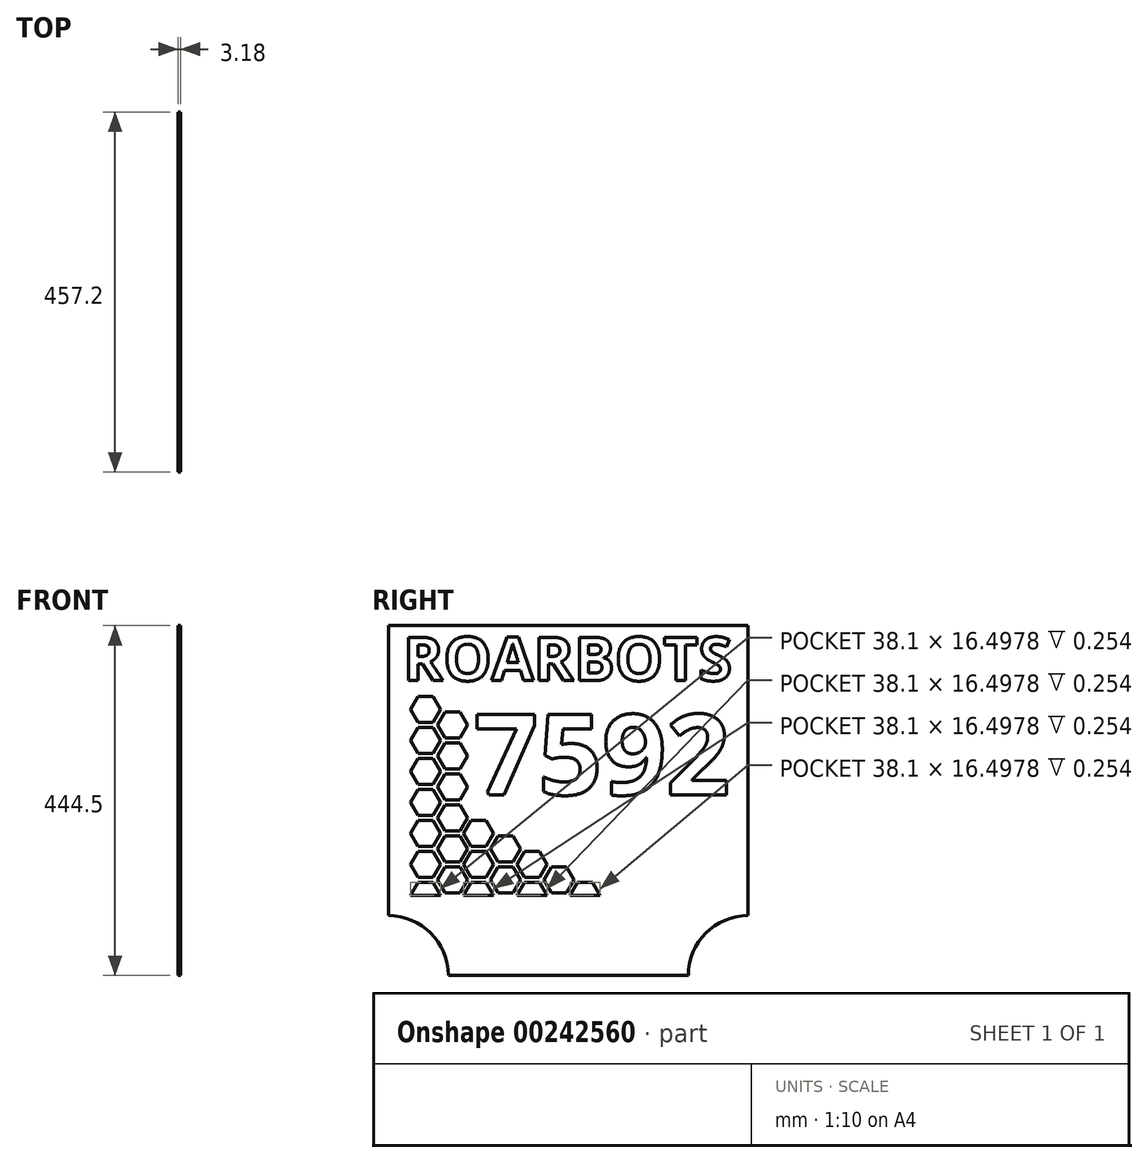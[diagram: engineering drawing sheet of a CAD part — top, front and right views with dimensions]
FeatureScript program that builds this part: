
annotation { "Feature Type Name" : "Feature", "Feature Type Description" : "" }
export const myFeature = defineFeature(function(context is Context, id is Id, definition is map)
    precondition{}
    {
        {
            var Q0;
            Q0=qCreatedBy(makeId("Right.planeOp"),FACE);
            var sketch = newSketch(context, id + "F0", { "sketchPlane" : qUnion([Q0])});
            skLineSegment(sketch, "E0.bottom", {"start": v(228.6, 222.25) * mm, "end": v(-228.6, 222.25) * mm, "construction": true});
            skLineSegment(sketch, "E0.top", {"start": v(228.6, -222.25) * mm, "end": v(-228.6, -222.25) * mm, "construction": true});
            skLineSegment(sketch, "E0.left", {"start": v(228.6, 222.25) * mm, "end": v(228.6, -222.25) * mm, "construction": true});
            skLineSegment(sketch, "E0.right", {"start": v(-228.6, 222.25) * mm, "end": v(-228.6, -222.25) * mm, "construction": true});
            skPoint(sketch, "E0.middle", {"position": v(0, 0) * mm});
            skLineSegment(sketch, "E1.bottom", {"start": v(-228.6, -222.25) * mm, "end": v(228.6, -222.25) * mm});
            skLineSegment(sketch, "E1.top", {"start": v(-228.6, 222.25) * mm, "end": v(228.6, 222.25) * mm});
            skLineSegment(sketch, "E1.left", {"start": v(-228.6, -222.25) * mm, "end": v(-228.6, 222.25) * mm});
            skLineSegment(sketch, "E1.right", {"start": v(228.6, -222.25) * mm, "end": v(228.6, 222.25) * mm});
            skCircle(sketch, "E2", {"center": v(-228.6, -222.25) * mm, "radius": 76.2 * mm});
            skCircle(sketch, "E3", {"center": v(228.6, -222.25) * mm, "radius": 76.2 * mm});
            skSolve(sketch);
        }
        {
            var Q0;
            {var subQ1=sQuery(id+"F0.wireOp",EDGE,"E1.top");Q0=makeQuery(id+"F0.imprint","IMPRINT",FACE,{"disambiguationData":[TD([[makeQuery(id+"F0.imprint","IMPRINT",EDGE,{"derivedFrom":subQ1}),-1.0]])]});}
            extrude(context, id + "F1", {"entities" : qUnion([Q0]), "depth" : 3.17 * mm});
        }
        {
            var Q0;
            Q0=makeQuery(id+"F1.opExtrude","CAP_FACE",FACE,{"disambiguationData":[OSD([sQuery(id+"F0.wireOp",EDGE,"E1.bottom"),sQuery(id+"F0.wireOp",EDGE,"E1.top"),sQuery(id+"F0.wireOp",EDGE,"E1.left"),sQuery(id+"F0.wireOp",EDGE,"E1.right")])],"isStart":false});
            var sketch = newSketch(context, id + "F2", { "sketchPlane" : qUnion([Q0])});
            skLineSegment(sketch, "E4", {"start": v(-228.6, -120.65) * mm, "end": v(228.6, -120.65) * mm});
            skCircle(sketch, "E5.cCircle", {"center": v(-181.28, -120.65) * mm, "radius": 19.05 * mm, "construction": true});
            skLineSegment(sketch, "E5.0", {"start": v(-162.23, -120.65) * mm, "end": v(-171.75, -137.15) * mm});
            skLineSegment(sketch, "E5.1", {"start": v(-171.75, -137.15) * mm, "end": v(-190.8, -137.15) * mm});
            skLineSegment(sketch, "E5.2", {"start": v(-190.8, -137.15) * mm, "end": v(-200.33, -120.65) * mm});
            skLineSegment(sketch, "E5.3", {"start": v(-200.33, -120.65) * mm, "end": v(-190.8, -104.15) * mm});
            skLineSegment(sketch, "E5.4", {"start": v(-190.8, -104.15) * mm, "end": v(-171.75, -104.15) * mm});
            skLineSegment(sketch, "E5.5", {"start": v(-171.75, -104.15) * mm, "end": v(-162.23, -120.65) * mm});
            skLineSegment(sketch, "E6", {"start": v(-228.6, -137.15) * mm, "end": v(228.6, -137.15) * mm});
            skCircle(sketch, "E7.cCircle", {"center": v(-147.2, -100.98) * mm, "radius": 19.05 * mm, "construction": true});
            skLineSegment(sketch, "E7.0", {"start": v(-137.68, -117.48) * mm, "end": v(-156.73, -117.48) * mm});
            skLineSegment(sketch, "E7.1", {"start": v(-156.73, -117.48) * mm, "end": v(-166.25, -100.98) * mm});
            skLineSegment(sketch, "E7.2", {"start": v(-166.25, -100.98) * mm, "end": v(-156.73, -84.48) * mm});
            skLineSegment(sketch, "E7.3", {"start": v(-156.73, -84.48) * mm, "end": v(-137.68, -84.48) * mm});
            skLineSegment(sketch, "E7.4", {"start": v(-137.68, -84.48) * mm, "end": v(-128.15, -100.98) * mm});
            skLineSegment(sketch, "E7.5", {"start": v(-128.15, -100.98) * mm, "end": v(-137.68, -117.48) * mm});
            skLineSegment(sketch, "E8", {"start": v(-181.28, -120.65) * mm, "end": v(-147.2, -100.98) * mm});
            skLineSegment(sketch, "E9.1.0.0", {"start": v(-94.66, -120.65) * mm, "end": v(-104.19, -137.15) * mm});
            skLineSegment(sketch, "E9.1.0.1", {"start": v(-104.19, -137.15) * mm, "end": v(-123.24, -137.15) * mm});
            skLineSegment(sketch, "E9.1.0.2", {"start": v(-123.24, -137.15) * mm, "end": v(-132.76, -120.65) * mm});
            skLineSegment(sketch, "E9.1.0.3", {"start": v(-132.76, -120.65) * mm, "end": v(-123.24, -104.15) * mm});
            skLineSegment(sketch, "E9.1.0.4", {"start": v(-123.24, -104.15) * mm, "end": v(-104.19, -104.15) * mm});
            skLineSegment(sketch, "E9.1.0.5", {"start": v(-104.19, -104.15) * mm, "end": v(-94.66, -120.65) * mm});
            skLineSegment(sketch, "E9.1.0.6", {"start": v(-70.11, -117.48) * mm, "end": v(-89.16, -117.48) * mm});
            skLineSegment(sketch, "E9.1.0.7", {"start": v(-89.16, -117.48) * mm, "end": v(-98.69, -100.98) * mm});
            skLineSegment(sketch, "E9.1.0.8", {"start": v(-98.69, -100.98) * mm, "end": v(-89.16, -84.48) * mm});
            skLineSegment(sketch, "E9.1.0.9", {"start": v(-89.16, -84.48) * mm, "end": v(-70.11, -84.48) * mm});
            skLineSegment(sketch, "E9.1.0.10", {"start": v(-70.11, -84.48) * mm, "end": v(-60.59, -100.98) * mm});
            skLineSegment(sketch, "E9.1.0.11", {"start": v(-60.59, -100.98) * mm, "end": v(-70.11, -117.48) * mm});
            skLineSegment(sketch, "E9.2.0.0", {"start": v(-27.1, -120.65) * mm, "end": v(-36.62, -137.15) * mm});
            skLineSegment(sketch, "E9.2.0.1", {"start": v(-36.62, -137.15) * mm, "end": v(-55.67, -137.15) * mm});
            skLineSegment(sketch, "E9.2.0.2", {"start": v(-55.67, -137.15) * mm, "end": v(-65.2, -120.65) * mm});
            skLineSegment(sketch, "E9.2.0.3", {"start": v(-65.2, -120.65) * mm, "end": v(-55.67, -104.15) * mm});
            skLineSegment(sketch, "E9.2.0.4", {"start": v(-55.67, -104.15) * mm, "end": v(-36.62, -104.15) * mm});
            skLineSegment(sketch, "E9.2.0.5", {"start": v(-36.62, -104.15) * mm, "end": v(-27.1, -120.65) * mm});
            skLineSegment(sketch, "E9.2.0.6", {"start": v(-2.55, -117.48) * mm, "end": v(-21.6, -117.48) * mm});
            skLineSegment(sketch, "E9.2.0.7", {"start": v(-21.6, -117.48) * mm, "end": v(-31.12, -100.98) * mm});
            skLineSegment(sketch, "E9.2.0.8", {"start": v(-31.12, -100.98) * mm, "end": v(-21.6, -84.48) * mm});
            skLineSegment(sketch, "E9.2.0.9", {"start": v(-21.6, -84.48) * mm, "end": v(-2.55, -84.48) * mm});
            skLineSegment(sketch, "E9.2.0.10", {"start": v(-2.55, -84.48) * mm, "end": v(6.98, -100.98) * mm});
            skLineSegment(sketch, "E9.2.0.11", {"start": v(6.98, -100.98) * mm, "end": v(-2.55, -117.48) * mm});
            skLineSegment(sketch, "E9.3.0.0", {"start": v(40.47, -120.65) * mm, "end": v(30.94, -137.15) * mm});
            skLineSegment(sketch, "E9.3.0.1", {"start": v(30.94, -137.15) * mm, "end": v(11.9, -137.15) * mm});
            skLineSegment(sketch, "E9.3.0.2", {"start": v(11.9, -137.15) * mm, "end": v(2.37, -120.65) * mm});
            skLineSegment(sketch, "E9.3.0.3", {"start": v(2.37, -120.65) * mm, "end": v(11.9, -104.15) * mm});
            skLineSegment(sketch, "E9.3.0.4", {"start": v(11.9, -104.15) * mm, "end": v(30.94, -104.15) * mm});
            skLineSegment(sketch, "E9.3.0.5", {"start": v(30.94, -104.15) * mm, "end": v(40.47, -120.65) * mm});
            skLineSegment(sketch, "E9.3.0.6", {"start": v(65.02, -117.48) * mm, "end": v(45.97, -117.48) * mm});
            skLineSegment(sketch, "E9.3.0.7", {"start": v(45.97, -117.48) * mm, "end": v(36.44, -100.98) * mm});
            skLineSegment(sketch, "E9.3.0.8", {"start": v(36.44, -100.98) * mm, "end": v(45.97, -84.48) * mm});
            skLineSegment(sketch, "E9.3.0.9", {"start": v(45.97, -84.48) * mm, "end": v(65.02, -84.48) * mm});
            skLineSegment(sketch, "E9.3.0.10", {"start": v(65.02, -84.48) * mm, "end": v(74.54, -100.98) * mm});
            skLineSegment(sketch, "E9.3.0.11", {"start": v(74.54, -100.98) * mm, "end": v(65.02, -117.48) * mm});
            skLineSegment(sketch, "E9.direction1", {"start": v(-171.75, -137.15) * mm, "end": v(-104.19, -137.15) * mm, "construction": true});
            skLineSegment(sketch, "E10.0.1.0", {"start": v(-162.23, -81.28) * mm, "end": v(-171.75, -97.78) * mm});
            skLineSegment(sketch, "E10.0.1.1", {"start": v(-190.8, -97.78) * mm, "end": v(-200.33, -81.28) * mm});
            skLineSegment(sketch, "E10.0.1.2", {"start": v(-200.33, -81.28) * mm, "end": v(-190.8, -64.78) * mm});
            skLineSegment(sketch, "E10.0.1.3", {"start": v(-190.8, -64.78) * mm, "end": v(-171.75, -64.78) * mm});
            skLineSegment(sketch, "E10.0.1.4", {"start": v(-171.75, -64.78) * mm, "end": v(-162.23, -81.28) * mm});
            skLineSegment(sketch, "E10.0.1.5", {"start": v(-137.68, -78.1) * mm, "end": v(-156.73, -78.1) * mm});
            skLineSegment(sketch, "E10.0.1.6", {"start": v(-156.73, -78.1) * mm, "end": v(-166.25, -61.6) * mm});
            skLineSegment(sketch, "E10.0.1.7", {"start": v(-166.25, -61.6) * mm, "end": v(-156.73, -45.1) * mm});
            skLineSegment(sketch, "E10.0.1.8", {"start": v(-156.73, -45.1) * mm, "end": v(-137.68, -45.1) * mm});
            skLineSegment(sketch, "E10.0.1.9", {"start": v(-137.68, -45.1) * mm, "end": v(-128.15, -61.6) * mm});
            skLineSegment(sketch, "E10.0.1.10", {"start": v(-128.15, -61.6) * mm, "end": v(-137.68, -78.1) * mm});
            skLineSegment(sketch, "E10.0.1.11", {"start": v(-132.76, -81.28) * mm, "end": v(-123.24, -64.78) * mm});
            skLineSegment(sketch, "E10.0.1.12", {"start": v(-123.24, -64.78) * mm, "end": v(-104.19, -64.78) * mm});
            skLineSegment(sketch, "E10.0.1.13", {"start": v(-104.19, -64.78) * mm, "end": v(-94.66, -81.28) * mm});
            skLineSegment(sketch, "E10.0.1.14", {"start": v(-94.66, -81.28) * mm, "end": v(-104.19, -97.78) * mm});
            skLineSegment(sketch, "E10.0.1.15", {"start": v(-123.24, -97.78) * mm, "end": v(-132.76, -81.28) * mm});
            skLineSegment(sketch, "E10.0.1.16", {"start": v(-89.16, -78.1) * mm, "end": v(-98.69, -61.6) * mm});
            skLineSegment(sketch, "E10.0.1.17", {"start": v(-98.69, -61.6) * mm, "end": v(-89.16, -45.1) * mm});
            skLineSegment(sketch, "E10.0.1.18", {"start": v(-89.16, -45.1) * mm, "end": v(-70.11, -45.1) * mm});
            skLineSegment(sketch, "E10.0.1.19", {"start": v(-70.11, -45.1) * mm, "end": v(-60.59, -61.6) * mm});
            skLineSegment(sketch, "E10.0.1.20", {"start": v(-60.59, -61.6) * mm, "end": v(-70.11, -78.1) * mm});
            skLineSegment(sketch, "E10.0.1.21", {"start": v(-70.11, -78.1) * mm, "end": v(-89.16, -78.1) * mm});
            skLineSegment(sketch, "E10.0.1.22", {"start": v(-55.67, -97.78) * mm, "end": v(-65.2, -81.28) * mm});
            skLineSegment(sketch, "E10.0.1.23", {"start": v(-65.2, -81.28) * mm, "end": v(-55.67, -64.78) * mm});
            skLineSegment(sketch, "E10.0.1.24", {"start": v(-55.67, -64.78) * mm, "end": v(-36.62, -64.78) * mm});
            skLineSegment(sketch, "E10.0.1.25", {"start": v(-36.62, -64.78) * mm, "end": v(-27.1, -81.28) * mm});
            skLineSegment(sketch, "E10.0.1.26", {"start": v(-27.1, -81.28) * mm, "end": v(-36.62, -97.78) * mm});
            skLineSegment(sketch, "E10.0.1.27", {"start": v(-21.6, -78.1) * mm, "end": v(-31.12, -61.6) * mm});
            skLineSegment(sketch, "E10.0.1.28", {"start": v(-31.12, -61.6) * mm, "end": v(-21.6, -45.1) * mm});
            skLineSegment(sketch, "E10.0.1.29", {"start": v(-21.6, -45.1) * mm, "end": v(-2.55, -45.1) * mm});
            skLineSegment(sketch, "E10.0.1.30", {"start": v(-2.55, -45.1) * mm, "end": v(6.98, -61.6) * mm});
            skLineSegment(sketch, "E10.0.1.31", {"start": v(6.98, -61.6) * mm, "end": v(-2.55, -78.1) * mm});
            skLineSegment(sketch, "E10.0.1.32", {"start": v(2.37, -81.28) * mm, "end": v(11.9, -64.78) * mm});
            skLineSegment(sketch, "E10.0.1.33", {"start": v(11.9, -64.78) * mm, "end": v(30.94, -64.78) * mm});
            skLineSegment(sketch, "E10.0.1.34", {"start": v(30.94, -64.78) * mm, "end": v(40.47, -81.28) * mm});
            skLineSegment(sketch, "E10.0.1.35", {"start": v(40.47, -81.28) * mm, "end": v(30.94, -97.78) * mm});
            skLineSegment(sketch, "E10.0.1.36", {"start": v(11.9, -97.78) * mm, "end": v(2.37, -81.28) * mm});
            skLineSegment(sketch, "E10.0.2.0", {"start": v(-162.23, -41.91) * mm, "end": v(-171.75, -58.4) * mm});
            skLineSegment(sketch, "E10.0.2.1", {"start": v(-190.8, -58.4) * mm, "end": v(-200.33, -41.91) * mm});
            skLineSegment(sketch, "E10.0.2.2", {"start": v(-200.33, -41.91) * mm, "end": v(-190.8, -25.41) * mm});
            skLineSegment(sketch, "E10.0.2.3", {"start": v(-190.8, -25.41) * mm, "end": v(-171.75, -25.41) * mm});
            skLineSegment(sketch, "E10.0.2.4", {"start": v(-171.75, -25.41) * mm, "end": v(-162.23, -41.91) * mm});
            skLineSegment(sketch, "E10.0.2.5", {"start": v(-137.68, -38.74) * mm, "end": v(-156.73, -38.74) * mm});
            skLineSegment(sketch, "E10.0.2.6", {"start": v(-156.73, -38.74) * mm, "end": v(-166.25, -22.24) * mm});
            skLineSegment(sketch, "E10.0.2.7", {"start": v(-166.25, -22.24) * mm, "end": v(-156.73, -5.74) * mm});
            skLineSegment(sketch, "E10.0.2.8", {"start": v(-156.73, -5.74) * mm, "end": v(-137.68, -5.74) * mm});
            skLineSegment(sketch, "E10.0.2.9", {"start": v(-137.68, -5.74) * mm, "end": v(-128.15, -22.24) * mm});
            skLineSegment(sketch, "E10.0.2.10", {"start": v(-128.15, -22.24) * mm, "end": v(-137.68, -38.74) * mm});
            skLineSegment(sketch, "E10.0.2.11", {"start": v(-132.76, -41.91) * mm, "end": v(-123.24, -25.41) * mm});
            skLineSegment(sketch, "E10.0.2.12", {"start": v(-123.24, -25.41) * mm, "end": v(-104.19, -25.41) * mm});
            skLineSegment(sketch, "E10.0.2.13", {"start": v(-104.19, -25.41) * mm, "end": v(-94.66, -41.91) * mm});
            skLineSegment(sketch, "E10.0.2.14", {"start": v(-94.66, -41.91) * mm, "end": v(-104.19, -58.4) * mm});
            skLineSegment(sketch, "E10.0.2.15", {"start": v(-123.24, -58.4) * mm, "end": v(-132.76, -41.9) * mm});
            skLineSegment(sketch, "E10.0.2.16", {"start": v(-89.16, -38.74) * mm, "end": v(-98.69, -22.24) * mm});
            skLineSegment(sketch, "E10.0.2.17", {"start": v(-98.69, -22.24) * mm, "end": v(-89.16, -5.74) * mm});
            skLineSegment(sketch, "E10.0.2.18", {"start": v(-89.16, -5.74) * mm, "end": v(-70.11, -5.74) * mm});
            skLineSegment(sketch, "E10.0.2.19", {"start": v(-70.11, -5.74) * mm, "end": v(-60.59, -22.24) * mm});
            skLineSegment(sketch, "E10.0.2.20", {"start": v(-60.59, -22.24) * mm, "end": v(-70.11, -38.74) * mm});
            skLineSegment(sketch, "E10.0.2.21", {"start": v(-70.11, -38.74) * mm, "end": v(-89.16, -38.74) * mm});
            skLineSegment(sketch, "E10.0.2.22", {"start": v(-55.67, -58.4) * mm, "end": v(-65.2, -41.9) * mm});
            skLineSegment(sketch, "E10.0.2.23", {"start": v(-65.2, -41.91) * mm, "end": v(-55.67, -25.41) * mm});
            skLineSegment(sketch, "E10.0.2.24", {"start": v(-55.67, -25.41) * mm, "end": v(-36.62, -25.41) * mm});
            skLineSegment(sketch, "E10.0.2.25", {"start": v(-36.62, -25.41) * mm, "end": v(-27.1, -41.91) * mm});
            skLineSegment(sketch, "E10.0.2.26", {"start": v(-27.1, -41.91) * mm, "end": v(-36.62, -58.4) * mm});
            skLineSegment(sketch, "E10.0.3.0", {"start": v(-162.23, -2.54) * mm, "end": v(-171.75, -19.04) * mm});
            skLineSegment(sketch, "E10.0.3.1", {"start": v(-190.8, -19.04) * mm, "end": v(-200.33, -2.54) * mm});
            skLineSegment(sketch, "E10.0.3.2", {"start": v(-200.33, -2.54) * mm, "end": v(-190.8, 13.96) * mm});
            skLineSegment(sketch, "E10.0.3.3", {"start": v(-190.8, 13.96) * mm, "end": v(-171.75, 13.96) * mm});
            skLineSegment(sketch, "E10.0.3.4", {"start": v(-171.75, 13.96) * mm, "end": v(-162.23, -2.54) * mm});
            skLineSegment(sketch, "E10.0.3.5", {"start": v(-137.68, 0.63) * mm, "end": v(-156.73, 0.63) * mm});
            skLineSegment(sketch, "E10.0.3.6", {"start": v(-156.73, 0.63) * mm, "end": v(-166.25, 17.13) * mm});
            skLineSegment(sketch, "E10.0.3.7", {"start": v(-166.25, 17.13) * mm, "end": v(-156.73, 33.63) * mm});
            skLineSegment(sketch, "E10.0.3.8", {"start": v(-156.73, 33.63) * mm, "end": v(-137.68, 33.63) * mm});
            skLineSegment(sketch, "E10.0.3.9", {"start": v(-137.68, 33.63) * mm, "end": v(-128.15, 17.13) * mm});
            skLineSegment(sketch, "E10.0.3.10", {"start": v(-128.15, 17.13) * mm, "end": v(-137.68, 0.63) * mm});
            skLineSegment(sketch, "E10.0.3.11", {"start": v(-132.76, -2.54) * mm, "end": v(-123.24, 13.96) * mm});
            skLineSegment(sketch, "E10.0.3.12", {"start": v(-123.24, 13.96) * mm, "end": v(-104.19, 13.96) * mm});
            skLineSegment(sketch, "E10.0.3.13", {"start": v(-104.19, 13.96) * mm, "end": v(-94.66, -2.54) * mm});
            skLineSegment(sketch, "E10.0.3.14", {"start": v(-94.66, -2.54) * mm, "end": v(-104.19, -19.04) * mm});
            skLineSegment(sketch, "E10.0.3.15", {"start": v(-123.24, -19.04) * mm, "end": v(-132.76, -2.54) * mm});
            skLineSegment(sketch, "E10.0.3.16", {"start": v(-89.16, 0.63) * mm, "end": v(-98.69, 17.13) * mm});
            skLineSegment(sketch, "E10.0.3.17", {"start": v(-98.69, 17.13) * mm, "end": v(-89.16, 33.63) * mm});
            skLineSegment(sketch, "E10.0.3.18", {"start": v(-89.16, 33.63) * mm, "end": v(-70.11, 33.63) * mm});
            skLineSegment(sketch, "E10.0.3.19", {"start": v(-70.11, 33.63) * mm, "end": v(-60.59, 17.13) * mm});
            skLineSegment(sketch, "E10.0.3.20", {"start": v(-60.59, 17.13) * mm, "end": v(-70.11, 0.63) * mm});
            skLineSegment(sketch, "E10.0.3.21", {"start": v(-70.11, 0.63) * mm, "end": v(-89.16, 0.63) * mm});
            skLineSegment(sketch, "E10.0.4.0", {"start": v(-162.23, 36.83) * mm, "end": v(-171.75, 20.33) * mm});
            skLineSegment(sketch, "E10.0.4.1", {"start": v(-190.8, 20.33) * mm, "end": v(-200.33, 36.83) * mm});
            skLineSegment(sketch, "E10.0.4.2", {"start": v(-200.33, 36.83) * mm, "end": v(-190.8, 53.33) * mm});
            skLineSegment(sketch, "E10.0.4.3", {"start": v(-190.8, 53.33) * mm, "end": v(-171.75, 53.33) * mm});
            skLineSegment(sketch, "E10.0.4.4", {"start": v(-171.75, 53.33) * mm, "end": v(-162.23, 36.83) * mm});
            skLineSegment(sketch, "E10.0.4.5", {"start": v(-137.68, 40) * mm, "end": v(-156.73, 40) * mm});
            skLineSegment(sketch, "E10.0.4.6", {"start": v(-156.73, 40) * mm, "end": v(-166.25, 56.5) * mm});
            skLineSegment(sketch, "E10.0.4.7", {"start": v(-166.25, 56.5) * mm, "end": v(-156.73, 73) * mm});
            skLineSegment(sketch, "E10.0.4.8", {"start": v(-156.73, 73) * mm, "end": v(-137.68, 73) * mm});
            skLineSegment(sketch, "E10.0.4.9", {"start": v(-137.68, 73) * mm, "end": v(-128.15, 56.5) * mm});
            skLineSegment(sketch, "E10.0.4.10", {"start": v(-128.15, 56.5) * mm, "end": v(-137.68, 40) * mm});
            skLineSegment(sketch, "E10.0.4.11", {"start": v(-132.76, 36.83) * mm, "end": v(-123.24, 53.33) * mm});
            skLineSegment(sketch, "E10.0.4.12", {"start": v(-123.24, 53.33) * mm, "end": v(-104.19, 53.33) * mm});
            skLineSegment(sketch, "E10.0.4.13", {"start": v(-104.19, 53.33) * mm, "end": v(-94.66, 36.83) * mm});
            skLineSegment(sketch, "E10.0.4.14", {"start": v(-94.66, 36.83) * mm, "end": v(-104.19, 20.33) * mm});
            skLineSegment(sketch, "E10.0.4.15", {"start": v(-123.24, 20.33) * mm, "end": v(-132.76, 36.83) * mm});
            skLineSegment(sketch, "E10.0.4.16", {"start": v(-89.16, 40) * mm, "end": v(-98.69, 56.5) * mm});
            skLineSegment(sketch, "E10.0.4.17", {"start": v(-98.69, 56.5) * mm, "end": v(-89.16, 73) * mm});
            skLineSegment(sketch, "E10.0.4.18", {"start": v(-89.16, 73) * mm, "end": v(-70.11, 73) * mm});
            skLineSegment(sketch, "E10.0.4.19", {"start": v(-70.11, 73) * mm, "end": v(-60.59, 56.5) * mm});
            skLineSegment(sketch, "E10.0.4.20", {"start": v(-60.59, 56.5) * mm, "end": v(-70.11, 40) * mm});
            skLineSegment(sketch, "E10.0.4.21", {"start": v(-70.11, 40) * mm, "end": v(-89.16, 40) * mm});
            skLineSegment(sketch, "E10.0.5.0", {"start": v(-162.23, 76.2) * mm, "end": v(-171.75, 59.7) * mm});
            skLineSegment(sketch, "E10.0.5.1", {"start": v(-190.8, 59.7) * mm, "end": v(-200.33, 76.2) * mm});
            skLineSegment(sketch, "E10.0.5.2", {"start": v(-200.33, 76.2) * mm, "end": v(-190.8, 92.7) * mm});
            skLineSegment(sketch, "E10.0.5.3", {"start": v(-190.8, 92.7) * mm, "end": v(-171.75, 92.7) * mm});
            skLineSegment(sketch, "E10.0.5.4", {"start": v(-171.75, 92.7) * mm, "end": v(-162.23, 76.2) * mm});
            skLineSegment(sketch, "E10.0.5.5", {"start": v(-137.68, 79.37) * mm, "end": v(-156.73, 79.37) * mm});
            skLineSegment(sketch, "E10.0.5.6", {"start": v(-156.73, 79.37) * mm, "end": v(-166.25, 95.87) * mm});
            skLineSegment(sketch, "E10.0.5.7", {"start": v(-166.25, 95.87) * mm, "end": v(-156.73, 112.37) * mm});
            skLineSegment(sketch, "E10.0.5.8", {"start": v(-156.73, 112.37) * mm, "end": v(-137.68, 112.37) * mm});
            skLineSegment(sketch, "E10.0.5.9", {"start": v(-137.68, 112.37) * mm, "end": v(-128.15, 95.87) * mm});
            skLineSegment(sketch, "E10.0.5.10", {"start": v(-128.15, 95.87) * mm, "end": v(-137.68, 79.37) * mm});
            skLineSegment(sketch, "E10.0.5.11", {"start": v(-132.76, 76.2) * mm, "end": v(-123.24, 92.7) * mm});
            skLineSegment(sketch, "E10.0.5.12", {"start": v(-123.24, 92.7) * mm, "end": v(-104.19, 92.7) * mm});
            skLineSegment(sketch, "E10.0.5.13", {"start": v(-104.19, 92.7) * mm, "end": v(-94.66, 76.2) * mm});
            skLineSegment(sketch, "E10.0.5.14", {"start": v(-94.66, 76.2) * mm, "end": v(-104.19, 59.7) * mm});
            skLineSegment(sketch, "E10.0.5.15", {"start": v(-123.24, 59.7) * mm, "end": v(-132.76, 76.2) * mm});
            skLineSegment(sketch, "E10.0.5.16", {"start": v(-89.16, 79.37) * mm, "end": v(-98.69, 95.87) * mm});
            skLineSegment(sketch, "E10.0.5.17", {"start": v(-98.69, 95.87) * mm, "end": v(-89.16, 112.37) * mm});
            skLineSegment(sketch, "E10.0.5.18", {"start": v(-89.16, 112.37) * mm, "end": v(-70.11, 112.37) * mm});
            skLineSegment(sketch, "E10.0.5.19", {"start": v(-70.11, 112.37) * mm, "end": v(-60.59, 95.87) * mm});
            skLineSegment(sketch, "E10.0.5.20", {"start": v(-60.59, 95.87) * mm, "end": v(-70.11, 79.37) * mm});
            skLineSegment(sketch, "E10.0.5.21", {"start": v(-70.11, 79.37) * mm, "end": v(-89.16, 79.37) * mm});
            skLineSegment(sketch, "E10.direction1", {"start": v(-171.75, -137.15) * mm, "end": v(31.7, -137.15) * mm, "construction": true});
            skLineSegment(sketch, "E10.direction2", {"start": v(-171.75, -137.15) * mm, "end": v(-171.75, -97.78) * mm, "construction": true});
            skLineSegment(sketch, "E11", {"start": v(-190.8, 59.7) * mm, "end": v(-171.75, 59.7) * mm});
            skLineSegment(sketch, "E12", {"start": v(-190.8, 20.33) * mm, "end": v(-171.75, 20.33) * mm});
            skLineSegment(sketch, "E13", {"start": v(-190.8, -19.04) * mm, "end": v(-171.75, -19.04) * mm});
            skLineSegment(sketch, "E14", {"start": v(-190.8, -58.4) * mm, "end": v(-171.75, -58.4) * mm});
            skLineSegment(sketch, "E15", {"start": v(-190.8, -97.78) * mm, "end": v(-171.75, -97.78) * mm});
            skLineSegment(sketch, "E16", {"start": v(-123.24, -97.78) * mm, "end": v(-104.19, -97.78) * mm});
            skLineSegment(sketch, "E17", {"start": v(-123.24, -58.4) * mm, "end": v(-104.19, -58.4) * mm});
            skLineSegment(sketch, "E18", {"start": v(-123.24, -19.04) * mm, "end": v(-104.19, -19.04) * mm});
            skLineSegment(sketch, "E19", {"start": v(-123.24, 20.33) * mm, "end": v(-104.19, 20.33) * mm});
            skLineSegment(sketch, "E20", {"start": v(-123.24, 59.7) * mm, "end": v(-104.19, 59.7) * mm});
            skLineSegment(sketch, "E21", {"start": v(-55.67, -97.78) * mm, "end": v(-36.62, -97.78) * mm});
            skLineSegment(sketch, "E22", {"start": v(-55.67, -58.4) * mm, "end": v(-36.62, -58.4) * mm});
            skLineSegment(sketch, "E23.0.0.6", {"start": v(-162.23, 115.57) * mm, "end": v(-171.75, 99.07) * mm});
            skLineSegment(sketch, "E23.3.0.6", {"start": v(-190.8, 99.07) * mm, "end": v(-200.33, 115.57) * mm});
            skLineSegment(sketch, "E23.6.0.6", {"start": v(-200.33, 115.57) * mm, "end": v(-190.8, 132.07) * mm});
            skLineSegment(sketch, "E23.9.0.6", {"start": v(-190.8, 132.07) * mm, "end": v(-171.75, 132.07) * mm});
            skLineSegment(sketch, "E23.12.0.6", {"start": v(-171.75, 132.07) * mm, "end": v(-162.23, 115.57) * mm});
            skLineSegment(sketch, "E23.15.0.6", {"start": v(-137.68, 118.74) * mm, "end": v(-156.73, 118.74) * mm});
            skLineSegment(sketch, "E23.18.0.6", {"start": v(-156.73, 118.74) * mm, "end": v(-166.25, 135.24) * mm});
            skLineSegment(sketch, "E23.21.0.6", {"start": v(-166.25, 135.24) * mm, "end": v(-156.73, 151.74) * mm});
            skLineSegment(sketch, "E23.24.0.6", {"start": v(-156.73, 151.74) * mm, "end": v(-137.68, 151.74) * mm});
            skLineSegment(sketch, "E23.27.0.6", {"start": v(-137.68, 151.74) * mm, "end": v(-128.15, 135.24) * mm});
            skLineSegment(sketch, "E23.30.0.6", {"start": v(-128.15, 135.24) * mm, "end": v(-137.68, 118.74) * mm});
            skLineSegment(sketch, "E23.33.0.6", {"start": v(-132.76, 115.57) * mm, "end": v(-123.24, 132.07) * mm});
            skLineSegment(sketch, "E23.36.0.6", {"start": v(-123.24, 132.07) * mm, "end": v(-104.19, 132.07) * mm});
            skLineSegment(sketch, "E23.39.0.6", {"start": v(-104.19, 132.07) * mm, "end": v(-94.66, 115.57) * mm});
            skLineSegment(sketch, "E23.42.0.6", {"start": v(-94.66, 115.57) * mm, "end": v(-104.19, 99.07) * mm});
            skLineSegment(sketch, "E23.45.0.6", {"start": v(-123.24, 99.07) * mm, "end": v(-132.76, 115.57) * mm});
            skLineSegment(sketch, "E23.48.0.6", {"start": v(-89.16, 118.74) * mm, "end": v(-98.69, 135.24) * mm});
            skLineSegment(sketch, "E23.51.0.6", {"start": v(-98.69, 135.24) * mm, "end": v(-89.16, 151.74) * mm});
            skLineSegment(sketch, "E23.54.0.6", {"start": v(-89.16, 151.74) * mm, "end": v(-70.11, 151.74) * mm});
            skLineSegment(sketch, "E23.57.0.6", {"start": v(-70.11, 151.74) * mm, "end": v(-60.59, 135.24) * mm});
            skLineSegment(sketch, "E23.60.0.6", {"start": v(-60.59, 135.24) * mm, "end": v(-70.11, 118.74) * mm});
            skLineSegment(sketch, "E23.63.0.6", {"start": v(-70.11, 118.74) * mm, "end": v(-89.16, 118.74) * mm});
            skLineSegment(sketch, "E24", {"start": v(-190.8, 99.07) * mm, "end": v(-171.75, 99.07) * mm});
            skLineSegment(sketch, "E25", {"start": v(-123.24, 99.07) * mm, "end": v(-104.19, 99.07) * mm});
            skLineSegment(sketch, "E26", {"start": v(-21.6, -78.1) * mm, "end": v(-2.55, -78.1) * mm});
            skLineSegment(sketch, "E27", {"start": v(11.9, -97.78) * mm, "end": v(30.94, -97.78) * mm});
            skCircle(sketch, "E28.cCircle", {"center": v(88.98, -120.65) * mm, "radius": 19.05 * mm, "construction": true});
            skLineSegment(sketch, "E28.0", {"start": v(98.5, -137.15) * mm, "end": v(79.46, -137.15) * mm});
            skLineSegment(sketch, "E28.1", {"start": v(79.46, -137.15) * mm, "end": v(69.93, -120.65) * mm});
            skLineSegment(sketch, "E28.2", {"start": v(69.93, -120.65) * mm, "end": v(79.46, -104.15) * mm});
            skLineSegment(sketch, "E28.3", {"start": v(79.46, -104.15) * mm, "end": v(98.5, -104.15) * mm});
            skLineSegment(sketch, "E28.4", {"start": v(98.5, -104.15) * mm, "end": v(108.03, -120.65) * mm});
            skLineSegment(sketch, "E28.5", {"start": v(108.03, -120.65) * mm, "end": v(98.5, -137.15) * mm});
            skText(sketch, "E29", { "text": "ROARBOTS", "fontName": "OpenSans-Bold.ttf"});
            skText(sketch, "E30", { "text": "7592", "fontName": "OpenSans-Bold.ttf"});
            const initialGuessF2  = {"E29": [-0.2098, 0.15224, 1, 0, 0.05564], "E30": [-0.11973, 0.00737, 1, 0, 0.10264]};
            skSetInitialGuess(sketch, initialGuessF2);
            skSolve(sketch);
        }
        {
            var Q0;
            {var subQ1=sQuery(id+"F2.wireOp",EDGE,"E5.3");Q0=makeQuery(id+"F2.imprint","IMPRINT",FACE,{"disambiguationData":[TD([[makeQuery(id+"F2.imprint","IMPRINT",EDGE,{"derivedFrom":subQ1}),-1.0]])]});}
            var Q1;
            {var subQ1=sQuery(id+"F2.wireOp",EDGE,"E4");var subQ3=sQuery(id+"F2.wireOp",EDGE,"E8");var subQ4=makeQuery(id+"F2.imprint","INTERSECT",VERTEX,{"derivedFrom":[subQ1,subQ3]});Q1=makeQuery(id+"F2.imprint","IMPRINT",FACE,{"disambiguationData":[TD([[makeQuery(id+"F2.imprint","IMPRINT",EDGE,{"disambiguationData":[TD([[subQ4,-1.0]])],"derivedFrom":subQ3}),-1.0]])]});}
            var Q2;
            {var subQ3=sQuery(id+"F2.wireOp",EDGE,"E7.0");Q2=makeQuery(id+"F2.imprint","IMPRINT",FACE,{"disambiguationData":[TD([[makeQuery(id+"F2.imprint","IMPRINT",EDGE,{"derivedFrom":subQ3}),-1.0]])]});}
            var Q3;
            {var subQ2=sQuery(id+"F2.wireOp",EDGE,"E9.1.0.3");Q3=makeQuery(id+"F2.imprint","IMPRINT",FACE,{"disambiguationData":[TD([[makeQuery(id+"F2.imprint","IMPRINT",EDGE,{"derivedFrom":subQ2}),-1.0]])]});}
            var Q4;
            Q4=makeQuery(id+"F2.imprint","IMPRINT",FACE,{"disambiguationData":[TD([[makeQuery(id+"F2.imprint","IMPRINT",EDGE,{"derivedFrom":sQuery(id+"F2.wireOp",EDGE,"E9.1.0.6")}),-1.0]])]});
            var Q5;
            {var subQ2=sQuery(id+"F2.wireOp",EDGE,"E9.2.0.3");Q5=makeQuery(id+"F2.imprint","IMPRINT",FACE,{"disambiguationData":[TD([[makeQuery(id+"F2.imprint","IMPRINT",EDGE,{"derivedFrom":subQ2}),-1.0]])]});}
            var Q6;
            Q6=makeQuery(id+"F2.imprint","IMPRINT",FACE,{"disambiguationData":[TD([[makeQuery(id+"F2.imprint","IMPRINT",EDGE,{"derivedFrom":sQuery(id+"F2.wireOp",EDGE,"E9.2.0.6")}),-1.0]])]});
            var Q7;
            {var subQ2=sQuery(id+"F2.wireOp",EDGE,"E9.3.0.3");Q7=makeQuery(id+"F2.imprint","IMPRINT",FACE,{"disambiguationData":[TD([[makeQuery(id+"F2.imprint","IMPRINT",EDGE,{"derivedFrom":subQ2}),-1.0]])]});}
            var Q8;
            Q8=makeQuery(id+"F2.imprint","IMPRINT",FACE,{"disambiguationData":[TD([[makeQuery(id+"F2.imprint","IMPRINT",EDGE,{"derivedFrom":sQuery(id+"F2.wireOp",EDGE,"E10.0.1.22")}),-1.0]])]});
            var Q9;
            Q9=makeQuery(id+"F2.imprint","IMPRINT",FACE,{"disambiguationData":[TD([[makeQuery(id+"F2.imprint","IMPRINT",EDGE,{"derivedFrom":sQuery(id+"F2.wireOp",EDGE,"E10.0.1.16")}),-1.0]])]});
            var Q10;
            Q10=makeQuery(id+"F2.imprint","IMPRINT",FACE,{"disambiguationData":[TD([[makeQuery(id+"F2.imprint","IMPRINT",EDGE,{"derivedFrom":sQuery(id+"F2.wireOp",EDGE,"E10.0.2.11")}),-1.0]])]});
            var Q11;
            Q11=makeQuery(id+"F2.imprint","IMPRINT",FACE,{"disambiguationData":[TD([[makeQuery(id+"F2.imprint","IMPRINT",EDGE,{"derivedFrom":sQuery(id+"F2.wireOp",EDGE,"E10.0.2.5")}),-1.0]])]});
            var Q12;
            Q12=makeQuery(id+"F2.imprint","IMPRINT",FACE,{"disambiguationData":[TD([[makeQuery(id+"F2.imprint","IMPRINT",EDGE,{"derivedFrom":sQuery(id+"F2.wireOp",EDGE,"E10.0.3.5")}),-1.0]])]});
            var Q13;
            Q13=makeQuery(id+"F2.imprint","IMPRINT",FACE,{"disambiguationData":[TD([[makeQuery(id+"F2.imprint","IMPRINT",EDGE,{"derivedFrom":sQuery(id+"F2.wireOp",EDGE,"E10.0.4.5")}),-1.0]])]});
            var Q14;
            Q14=makeQuery(id+"F2.imprint","IMPRINT",FACE,{"disambiguationData":[TD([[makeQuery(id+"F2.imprint","IMPRINT",EDGE,{"derivedFrom":sQuery(id+"F2.wireOp",EDGE,"E10.0.5.5")}),-1.0]])]});
            var Q15;
            Q15=makeQuery(id+"F2.imprint","IMPRINT",FACE,{"disambiguationData":[TD([[makeQuery(id+"F2.imprint","IMPRINT",EDGE,{"derivedFrom":sQuery(id+"F2.wireOp",EDGE,"E23.0.0.6")}),-1.0]])]});
            var Q16;
            Q16=makeQuery(id+"F2.imprint","IMPRINT",FACE,{"disambiguationData":[TD([[makeQuery(id+"F2.imprint","IMPRINT",EDGE,{"derivedFrom":sQuery(id+"F2.wireOp",EDGE,"E10.0.5.0")}),-1.0]])]});
            var Q17;
            Q17=makeQuery(id+"F2.imprint","IMPRINT",FACE,{"disambiguationData":[TD([[makeQuery(id+"F2.imprint","IMPRINT",EDGE,{"derivedFrom":sQuery(id+"F2.wireOp",EDGE,"E10.0.4.0")}),-1.0]])]});
            var Q18;
            Q18=makeQuery(id+"F2.imprint","IMPRINT",FACE,{"disambiguationData":[TD([[makeQuery(id+"F2.imprint","IMPRINT",EDGE,{"derivedFrom":sQuery(id+"F2.wireOp",EDGE,"E10.0.3.0")}),-1.0]])]});
            var Q19;
            Q19=makeQuery(id+"F2.imprint","IMPRINT",FACE,{"disambiguationData":[TD([[makeQuery(id+"F2.imprint","IMPRINT",EDGE,{"derivedFrom":sQuery(id+"F2.wireOp",EDGE,"E10.0.2.0")}),-1.0]])]});
            var Q20;
            Q20=makeQuery(id+"F2.imprint","IMPRINT",FACE,{"disambiguationData":[TD([[makeQuery(id+"F2.imprint","IMPRINT",EDGE,{"derivedFrom":sQuery(id+"F2.wireOp",EDGE,"E10.0.1.0")}),-1.0]])]});
            var Q21;
            Q21=makeQuery(id+"F2.imprint","IMPRINT",FACE,{"disambiguationData":[TD([[makeQuery(id+"F2.imprint","IMPRINT",EDGE,{"derivedFrom":sQuery(id+"F2.wireOp",EDGE,"E10.0.1.5")}),-1.0]])]});
            var Q22;
            Q22=makeQuery(id+"F2.imprint","IMPRINT",FACE,{"disambiguationData":[TD([[makeQuery(id+"F2.imprint","IMPRINT",EDGE,{"derivedFrom":sQuery(id+"F2.wireOp",EDGE,"E10.0.1.11")}),-1.0]])]});
            var Q23;
            {var subQ20=sQuery(id+"F2.wireOp",EDGE,"E10.0.3.17");Q23=makeQuery(id+"F2.imprint","IMPRINT",FACE,{"disambiguationData":[TD([[makeQuery(id+"F2.imprint","IMPRINT",EDGE,{"derivedFrom":subQ20}),1.0]])]});}
            var Q24;
            {var subQ4=sQuery(id+"F2.wireOp",EDGE,"E10.0.3.17");Q24=makeQuery(id+"F2.imprint","IMPRINT",FACE,{"disambiguationData":[TD([[makeQuery(id+"F2.imprint","IMPRINT",EDGE,{"derivedFrom":subQ4}),-1.0]])]});}
            var Q25;
            {var subQ4=sQuery(id+"F2.wireOp",EDGE,"E10.0.4.19");Q25=makeQuery(id+"F2.imprint","IMPRINT",FACE,{"disambiguationData":[TD([[makeQuery(id+"F2.imprint","IMPRINT",EDGE,{"derivedFrom":subQ4}),-1.0]])]});}
            var Q26;
            {var subQ0=sQuery(id+"F2.wireOp",EDGE,"E10.0.5.20");Q26=makeQuery(id+"F2.imprint","IMPRINT",FACE,{"disambiguationData":[TD([[makeQuery(id+"F2.imprint","IMPRINT",EDGE,{"derivedFrom":subQ0}),-1.0]])]});}
            var Q27;
            {var subQ7=sQuery(id+"F2.wireOp",EDGE,"E10.0.5.13");var subQ8=sQuery(id+"F2.wireOp",EDGE,"E10.0.5.12");var subQ9=makeQuery(id+"F2.imprint","INTERSECT",VERTEX,{"derivedFrom":[subQ8,subQ7]});Q27=makeQuery(id+"F2.imprint","IMPRINT",FACE,{"disambiguationData":[TD([[makeQuery(id+"F2.imprint","IMPRINT",EDGE,{"disambiguationData":[TD([[subQ9,1.0]])],"derivedFrom":subQ8}),1.0]])]});}
            var Q28;
            {var subQ0=sQuery(id+"F2.wireOp",EDGE,"E25");var subQ1=sQuery(id+"F2.wireOp",EDGE,"E23.42.0.6");var subQ2=makeQuery(id+"F2.imprint","INTERSECT",VERTEX,{"derivedFrom":[subQ1,subQ0]});Q28=makeQuery(id+"F2.imprint","IMPRINT",FACE,{"disambiguationData":[TD([[makeQuery(id+"F2.imprint","IMPRINT",EDGE,{"disambiguationData":[TD([[subQ2,1.0]])],"derivedFrom":subQ1}),-1.0]])]});}
            var Q29;
            {var subQ0=sQuery(id+"F2.wireOp",EDGE,"E10.0.5.13");var subQ1=sQuery(id+"F2.wireOp",EDGE,"E10.0.5.12");var subQ2=makeQuery(id+"F2.imprint","INTERSECT",VERTEX,{"derivedFrom":[subQ1,subQ0]});Q29=makeQuery(id+"F2.imprint","IMPRINT",FACE,{"disambiguationData":[TD([[makeQuery(id+"F2.imprint","IMPRINT",EDGE,{"disambiguationData":[TD([[subQ2,1.0]])],"derivedFrom":subQ1}),-1.0]])]});}
            var Q30;
            Q30=makeQuery(id+"F2.imprint","IMPRINT",FACE,{"disambiguationData":[TD([[makeQuery(id+"F2.imprint","IMPRINT",EDGE,{"derivedFrom":sQuery(id+"F2.wireOp",EDGE,"E30.sketch_text.stroke-7")}),-1.0]])]});
            var Q31;
            Q31=makeQuery(id+"F2.imprint","IMPRINT",FACE,{"disambiguationData":[TD([[makeQuery(id+"F2.imprint","IMPRINT",EDGE,{"derivedFrom":sQuery(id+"F2.wireOp",EDGE,"E30.sketch_text.stroke-27")}),-1.0]])]});
            var Q32;
            Q32=makeQuery(id+"F2.imprint","IMPRINT",FACE,{"disambiguationData":[TD([[makeQuery(id+"F2.imprint","IMPRINT",EDGE,{"derivedFrom":sQuery(id+"F2.wireOp",EDGE,"E30.sketch_text.stroke-53")}),-1.0]])]});
            var Q33;
            Q33=makeQuery(id+"F2.imprint","IMPRINT",FACE,{"disambiguationData":[TD([[makeQuery(id+"F2.imprint","IMPRINT",EDGE,{"derivedFrom":sQuery(id+"F2.wireOp",EDGE,"E29.sketch_text.stroke-111")}),-1.0]])]});
            var Q34;
            Q34=makeQuery(id+"F2.imprint","IMPRINT",FACE,{"disambiguationData":[TD([[makeQuery(id+"F2.imprint","IMPRINT",EDGE,{"derivedFrom":sQuery(id+"F2.wireOp",EDGE,"E29.sketch_text.stroke-103")}),-1.0]])]});
            var Q35;
            Q35=makeQuery(id+"F2.imprint","IMPRINT",FACE,{"disambiguationData":[TD([[makeQuery(id+"F2.imprint","IMPRINT",EDGE,{"derivedFrom":sQuery(id+"F2.wireOp",EDGE,"E29.sketch_text.stroke-89")}),-1.0]])]});
            var Q36;
            Q36=makeQuery(id+"F2.imprint","IMPRINT",FACE,{"disambiguationData":[TD([[makeQuery(id+"F2.imprint","IMPRINT",EDGE,{"derivedFrom":sQuery(id+"F2.wireOp",EDGE,"E29.sketch_text.stroke-64")}),-1.0]])]});
            var Q37;
            Q37=makeQuery(id+"F2.imprint","IMPRINT",FACE,{"disambiguationData":[TD([[makeQuery(id+"F2.imprint","IMPRINT",EDGE,{"derivedFrom":sQuery(id+"F2.wireOp",EDGE,"E29.sketch_text.stroke-45")}),-1.0]])]});
            var Q38;
            Q38=makeQuery(id+"F2.imprint","IMPRINT",FACE,{"disambiguationData":[TD([[makeQuery(id+"F2.imprint","IMPRINT",EDGE,{"derivedFrom":sQuery(id+"F2.wireOp",EDGE,"E29.sketch_text.stroke-33")}),-1.0]])]});
            var Q39;
            Q39=makeQuery(id+"F2.imprint","IMPRINT",FACE,{"disambiguationData":[TD([[makeQuery(id+"F2.imprint","IMPRINT",EDGE,{"derivedFrom":sQuery(id+"F2.wireOp",EDGE,"E29.sketch_text.stroke-19")}),-1.0]])]});
            var Q40;
            Q40=makeQuery(id+"F2.imprint","IMPRINT",FACE,{"disambiguationData":[TD([[makeQuery(id+"F2.imprint","IMPRINT",EDGE,{"derivedFrom":sQuery(id+"F2.wireOp",EDGE,"E29.sketch_text.stroke-0")}),-1.0]])]});
            extrude(context, id + "F3", {"entities" : qUnion([Q0, Q1, Q2, Q3, Q4, Q5, Q6, Q7, Q8, Q9, Q10, Q11, Q12, Q13, Q14, Q15, Q16, Q17, Q18, Q19, Q20, Q21, Q22, Q23, Q24, Q25, Q26, Q27, Q28, Q29, Q30, Q31, Q32, Q33, Q34, Q35, Q36, Q37, Q38, Q39, Q40]), "operationType" : NewBodyOperationType.REMOVE, "oppositeDirection" : true, "depth" : 0.25 * mm});
        }
    });
